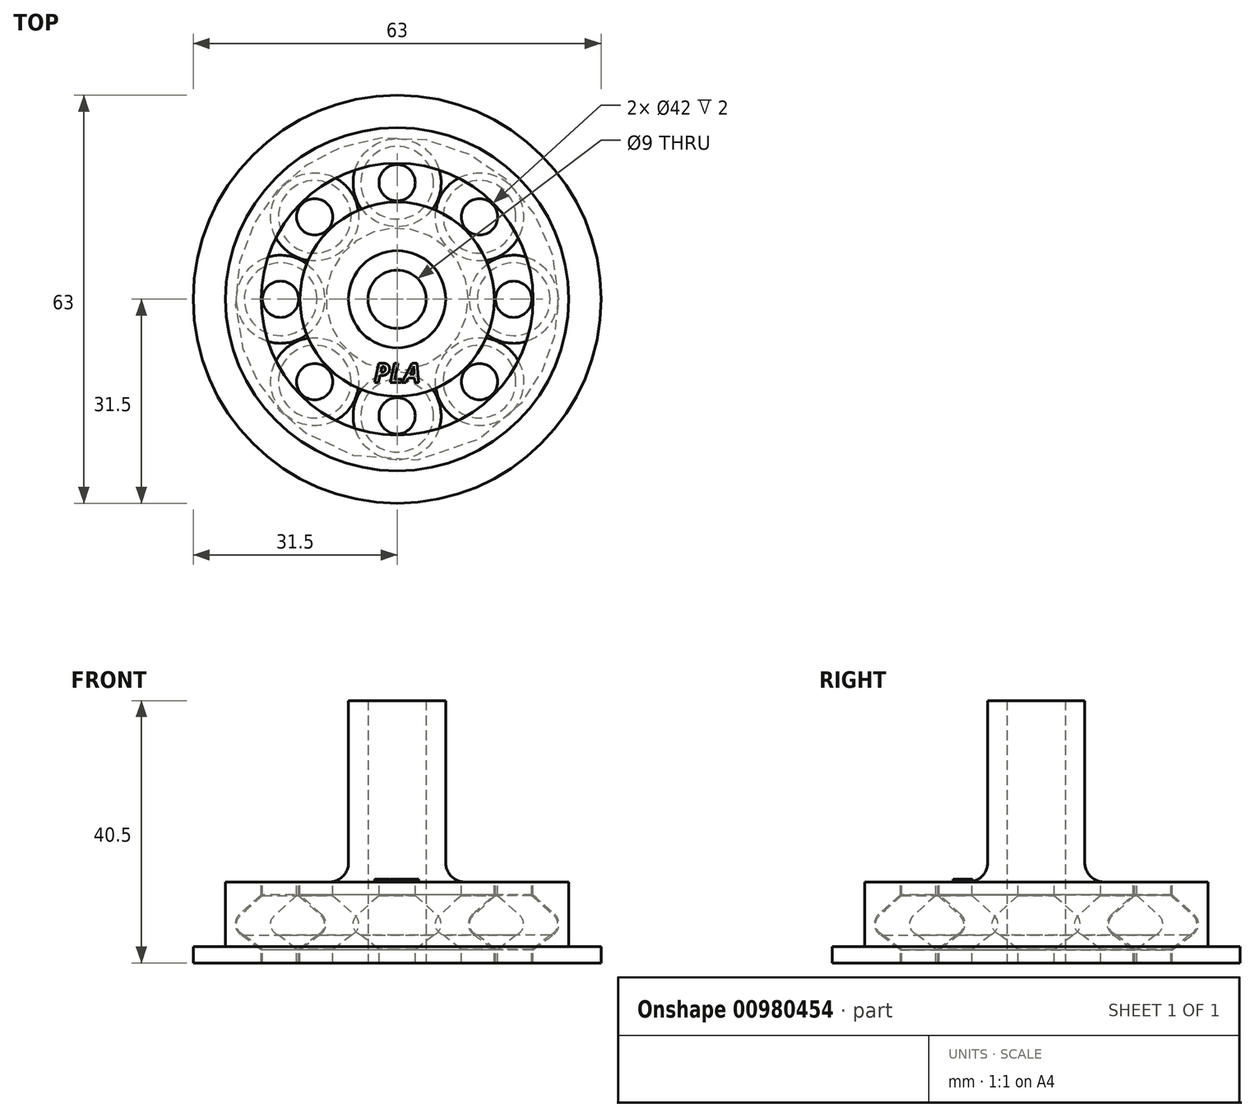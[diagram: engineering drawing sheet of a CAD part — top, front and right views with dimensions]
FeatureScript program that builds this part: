
annotation { "Feature Type Name" : "Feature", "Feature Type Description" : "" }
export const myFeature = defineFeature(function(context is Context, id is Id, definition is map)
    precondition{}
    {
        {
            var Q0;
            Q0=qCreatedBy(makeId("Top.planeOp"),FACE);
            var sketch = newSketch(context, id + "F0", { "sketchPlane" : qUnion([Q0])});
            skCircle(sketch, "E0", {"center": v(0, 0) * mm, "radius": 26.5 * mm});
            skSolve(sketch);
        }
        {
            var Q0;
            Q0=qSketchRegion(id+"F0",true);
            extrude(context, id + "F1", {"entities" : qUnion([Q0]), "depth" : 38 * mm, "offsetDistance" : 25 * mm});
        }
        {
            var Q0;
            Q0=qCreatedBy(makeId("Top.planeOp"),FACE);
            var sketch = newSketch(context, id + "F2", { "sketchPlane" : qUnion([Q0])});
            skCircle(sketch, "E1.0", {"center": v(0, 0) * mm, "radius": 31.5 * mm});
            skSolve(sketch);
        }
        {
            var Q0;
            Q0=qSketchRegion(id+"F2",true);
            extrude(context, id + "F3", {"entities" : qUnion([Q0]), "operationType" : NewBodyOperationType.ADD, "oppositeDirection" : true, "depth" : 2.5 * mm, "offsetDistance" : 25 * mm});
        }
        {
            var Q0;
            Q0=makeQuery(id+"F3.opExtrude","CAP_FACE",FACE,{"disambiguationData":[OSD([sQuery(id+"F2.wireOp",EDGE,"E1.0")])],"isStart":false});
            var sketch = newSketch(context, id + "F4", { "sketchPlane" : qUnion([Q0])});
            skPoint(sketch, "E2", {"position": v(0, 0) * mm});
            skSolve(sketch);
        }
        {
            var Q0;
            Q0=sQuery(id+"F4.wireOp",VERTEX,"E2");
            var Q1;
            Q1=makeQuery(id+"F1.opExtrude","SWEPT_BODY",BODY,{"disambiguationData":[OSD([sQuery(id+"F0.wireOp",EDGE,"E0")])]});
            hole(context, id + "F5", {"style" : HoleStyle.SIMPLE, "endStyle" : HoleEndStyle.THROUGH, "standardTappedOrClearance" : lookupTablePath({ "standard" : "ISO", "fit" : "Normal", "size" : "M8", "type" : "Clearance" }), "standardBlindInLast" : lookupTablePath({ "fit" : "Normal", "standard" : "ISO", "engagement" : "75%", "pitch" : "1.25 mm", "size" : "M8", "type" : "Clearance & tapped" }), "holeDiameter" : 9 * mm, "majorDiameter" : 5 * mm, "isTappedThrough" : true, "tappedDepth" : 12 * mm, "tapClearance" : 3, "locations" : qUnion([Q0]), "scope" : qUnion([Q1])});
        }
        {
            var Q0;
            Q0=qCreatedBy(makeId("Top.planeOp"),FACE);
            cPlane(context, id + "F6", {"entities" : qUnion([Q0]), "cplaneType" : CPlaneType.OFFSET, "offset" : 10 * mm, "width" : 150 * mm, "height" : 150 * mm});
        }
        {
            var Q0;
            Q0=qCreatedBy(id+"F6.planeOp",FACE);
            var sketch = newSketch(context, id + "F7", { "sketchPlane" : qUnion([Q0])});
            skCircle(sketch, "E3.0", {"center": v(0, 0) * mm, "radius": 7.5 * mm});
            skCircle(sketch, "E4.0", {"center": v(0, 0) * mm, "radius": 26.5 * mm});
            skSolve(sketch);
        }
        {
            var Q0;
            Q0=qSketchRegion(id+"F7",true);
            extrude(context, id + "F8", {"entities" : qUnion([Q0]), "operationType" : NewBodyOperationType.REMOVE, "endBound" : BoundingType.THROUGH_ALL, "depth" : 25 * mm, "offsetDistance" : 25 * mm});
        }
        {
            var Q0;
            Q0=qCreatedBy(makeId("Front.planeOp"),FACE);
            var sketch = newSketch(context, id + "F9", { "sketchPlane" : qUnion([Q0])});
            skLineSegment(sketch, "E5", {"start": v(0, 0) * mm, "end": v(0, 60.57) * mm, "construction": true});
            skSolve(sketch);
        }
        {
            var Q0;
            Q0=qCreatedBy(makeId("Front.planeOp"),FACE);
            var sketch = newSketch(context, id + "F10", { "sketchPlane" : qUnion([Q0])});
            skArc(sketch, "E6", {"start": v(11.66, 4.98) * mm, "mid": v(11, 3.4) * mm, "end": v(11.8, 1.9) * mm});
            skLineSegment(sketch, "E7", {"start": v(15, -2.5) * mm, "end": v(15, -0.5) * mm});
            skLineSegment(sketch, "E8", {"start": v(18, 15.03) * mm, "end": v(18, -8.08) * mm, "construction": true});
            skArc(sketch, "E9.MirrorCS", {"start": v(24.34, 4.98) * mm, "mid": v(25, 3.4) * mm, "end": v(24.2, 1.9) * mm});
            skLineSegment(sketch, "E10", {"start": v(15, 10) * mm, "end": v(21, 10) * mm});
            skLineSegment(sketch, "E11", {"start": v(15, -2.5) * mm, "end": v(21, -2.5) * mm});
            skLineSegment(sketch, "E12", {"start": v(21, 10) * mm, "end": v(21, 8) * mm});
            skLineSegment(sketch, "E13", {"start": v(11.66, 4.98) * mm, "end": v(15, 8) * mm});
            skLineSegment(sketch, "E14", {"start": v(11.8, 1.9) * mm, "end": v(15, -0.5) * mm});
            skLineSegment(sketch, "E15", {"start": v(24.34, 4.98) * mm, "end": v(21, 8) * mm});
            skLineSegment(sketch, "E16", {"start": v(24.2, 1.9) * mm, "end": v(21, -0.5) * mm});
            skLineSegment(sketch, "E17.trimOffspring", {"start": v(15, 8) * mm, "end": v(15, 10) * mm});
            skLineSegment(sketch, "E18.trimOffspring", {"start": v(21, -0.5) * mm, "end": v(21, -2.5) * mm});
            skSolve(sketch);
        }
        {
            var Q0;
            Q0=qSketchRegion(id+"F10",true);
            var Q1;
            Q1=sQuery(id+"F9.wireOp",EDGE,"E5");
            revolve(context, id + "F11", {"operationType" : NewBodyOperationType.REMOVE, "surfaceOperationType" : NewSurfaceOperationType.NEW, "entities" : qUnion([Q0]), "axis" : qUnion([Q1]), "revolveType" : RevolveType.FULL, "oppositeDirection" : true});
        }
        {
            var Q0;
            Q0=qCreatedBy(makeId("Front.planeOp"),FACE);
            var sketch = newSketch(context, id + "F12", { "sketchPlane" : qUnion([Q0])});
            skPoint(sketch, "E19.orphan", {"position": v(19.41, 10) * mm});
            skPoint(sketch, "E20.orphan", {"position": v(14.59, 10) * mm});
            skPoint(sketch, "E21.end.orphan", {"position": v(17, 3.75) * mm});
            skPoint(sketch, "E22.orphan", {"position": v(20.15, 10) * mm});
            skPoint(sketch, "E23.orphan", {"position": v(17, 10) * mm});
            skPoint(sketch, "E24.start.orphan", {"position": v(13.85, -2.5) * mm});
            skArc(sketch, "E25.1", {"start": v(11.8, 4.84) * mm, "mid": v(11.23, 3.15) * mm, "end": v(12.39, 1.8) * mm});
            skLineSegment(sketch, "E26", {"start": v(15.2, 10) * mm, "end": v(18, 10) * mm});
            skLineSegment(sketch, "E27", {"start": v(15.2, -2.5) * mm, "end": v(18, -2.5) * mm});
            skLineSegment(sketch, "E28", {"start": v(18, 10) * mm, "end": v(18, -2.5) * mm});
            skLineSegment(sketch, "E29", {"start": v(15.2, 10) * mm, "end": v(15.2, 7.91) * mm});
            skLineSegment(sketch, "E30", {"start": v(15.2, 7.91) * mm, "end": v(11.8, 4.84) * mm});
            skLineSegment(sketch, "E31", {"start": v(12.39, 1.8) * mm, "end": v(15.2, -0.41) * mm});
            skLineSegment(sketch, "E32", {"start": v(15.2, -0.41) * mm, "end": v(15.2, -2.5) * mm});
            skSolve(sketch);
        }
        {
            var Q0;
            Q0=qSketchRegion(id+"F12",true);
            var Q1;
            Q1=sQuery(id+"F10.wireOp",EDGE,"E8");
            revolve(context, id + "F13", {"surfaceOperationType" : NewSurfaceOperationType.NEW, "entities" : qUnion([Q0]), "axis" : qUnion([Q1]), "revolveType" : RevolveType.FULL});
        }
        {
            var Q0;
            Q0=makeQuery(id+"F13.opRevolve","SWEPT_BODY",BODY,{"disambiguationData":[OSD([sQuery(id+"F12.wireOp",EDGE,"E25.0"),sQuery(id+"F12.wireOp",EDGE,"E25.1"),sQuery(id+"F12.wireOp",EDGE,"E25.2"),sQuery(id+"F12.wireOp",EDGE,"E26"),sQuery(id+"F12.wireOp",EDGE,"E27"),sQuery(id+"F12.wireOp",EDGE,"E28")])]});
            var Q1;
            Q1=sQuery(id+"F9.wireOp",EDGE,"E5");
            circularPattern(context, id + "F14", {"entities" : qUnion([Q0]), "axis" : qUnion([Q1]), "angle" : 360 * degree, "instanceCount" : 8, "equalSpace" : true});
        }
        {
            var Q0;
            Q0=makeQuery(id+"F8.boolean.opBoolean","COPY",EDGE,{"derivedFrom":makeQuery(id+"F8.opExtrude","CAP_EDGE",EDGE,{"disambiguationData":[OSD([sQuery(id+"F7.wireOp",EDGE,"E3.0")])],"isStart":true})});
            fillet(context, id + "F15", {"entities" : qUnion([Q0]), "radius" : 3 * mm, "tangentPropagation" : true, "allowEdgeOverflow" : false});
        }
        {
            var Q0;
            {var subQ0=sQuery(id+"F7.wireOp",EDGE,"E3.0");Q0=makeQuery(id+"F11.boolean.opBoolean","SPLIT",FACE,{"disambiguationData":[TD([makeQuery(id+"F8.boolean.opBoolean","COPY",FACE,{"derivedFrom":makeQuery(id+"F8.opExtrude","SWEPT_FACE",FACE,{"disambiguationData":[OSD([subQ0])]})})])],"derivedFrom":makeQuery(id+"F8.boolean.opBoolean","COPY",FACE,{"derivedFrom":makeQuery(id+"F8.opExtrude","CAP_FACE",FACE,{"disambiguationData":[OSD([subQ0,sQuery(id+"F7.wireOp",EDGE,"E4.0")])],"isStart":true})})});}
            var sketch = newSketch(context, id + "F16", { "sketchPlane" : qUnion([Q0])});
            skText(sketch, "E33", { "text": "PLA", "fontName": "OpenSans-BoldItalic.ttf"});
            const initialGuessF16  = {"E33": [-0.0036, -0.01286, 1, 0, 0.003]};
            skSetInitialGuess(sketch, initialGuessF16);
            skSolve(sketch);
        }
        {
            var Q0;
            Q0 = qSketchRegion(id + "F16", true);
            extrude(context, id + "F17", {"entities" : qUnion([Q0]), "operationType" : NewBodyOperationType.ADD, "depth" : 0.4 * mm, "offsetDistance" : 25 * mm});
        }
    });
